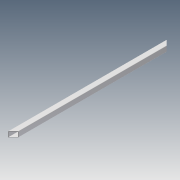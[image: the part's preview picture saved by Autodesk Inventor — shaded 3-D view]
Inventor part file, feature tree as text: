
AUTODESK INVENTOR PART (.ipt)
format: ipt  version: 2014 (Build 180170000, 170)  size: 113,152 bytes
history: native  units: in
note: dims shown in document units (in); Inventor stores cm internally (conversion verified against a paired STEP export)
features: extrude x2, sketch x2
ambient origin geometry x8: Origin, YZ Plane, XZ Plane, XY Plane, X Axis, Y Axis, Z Axis, Center Point
bodies: Solid1 (feature_tree)
feature tree (4):
  extrude  "Extrusion1"  Depth=1.0in
  extrude  "Extrusion2"  Depth=0.063in
  sketch  "Sketch1"  dims[d0=1.0in d1=1.0in]
  sketch  "Sketch2"  dims[d2=0.07in d3=0.063in d4=29.5in d5=0.0in d7=45.0deg d9=45.0deg d10=1.0in d11=0.0in]
